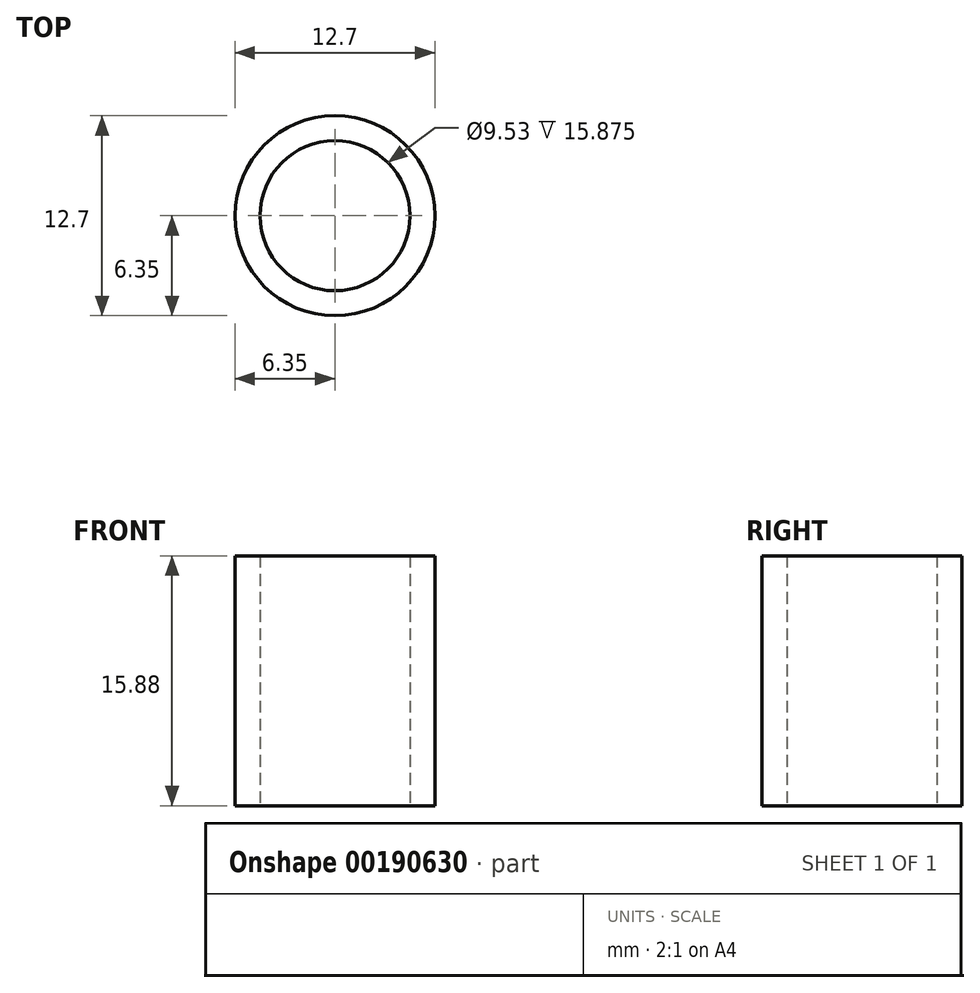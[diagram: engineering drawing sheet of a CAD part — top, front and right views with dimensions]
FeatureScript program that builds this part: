
annotation { "Feature Type Name" : "Feature", "Feature Type Description" : "" }
export const myFeature = defineFeature(function(context is Context, id is Id, definition is map)
    precondition{}
    {
        {
            var Q0;
            Q0=qCreatedBy(makeId("Top.planeOp"),FACE);
            var sketch = newSketch(context, id + "F0", { "sketchPlane" : qUnion([Q0])});
            skCircle(sketch, "E0", {"center": v(0, 0) * mm, "radius": 6.35 * mm});
            skCircle(sketch, "E1", {"center": v(0, 0) * mm, "radius": 4.76 * mm});
            skSolve(sketch);
        }
        {
            var Q0;
            Q0 = qSketchRegion(id + "F0", true);
            extrude(context, id + "F1", {"entities" : qUnion([Q0]), "depth" : 15.88 * mm});
        }
    });
